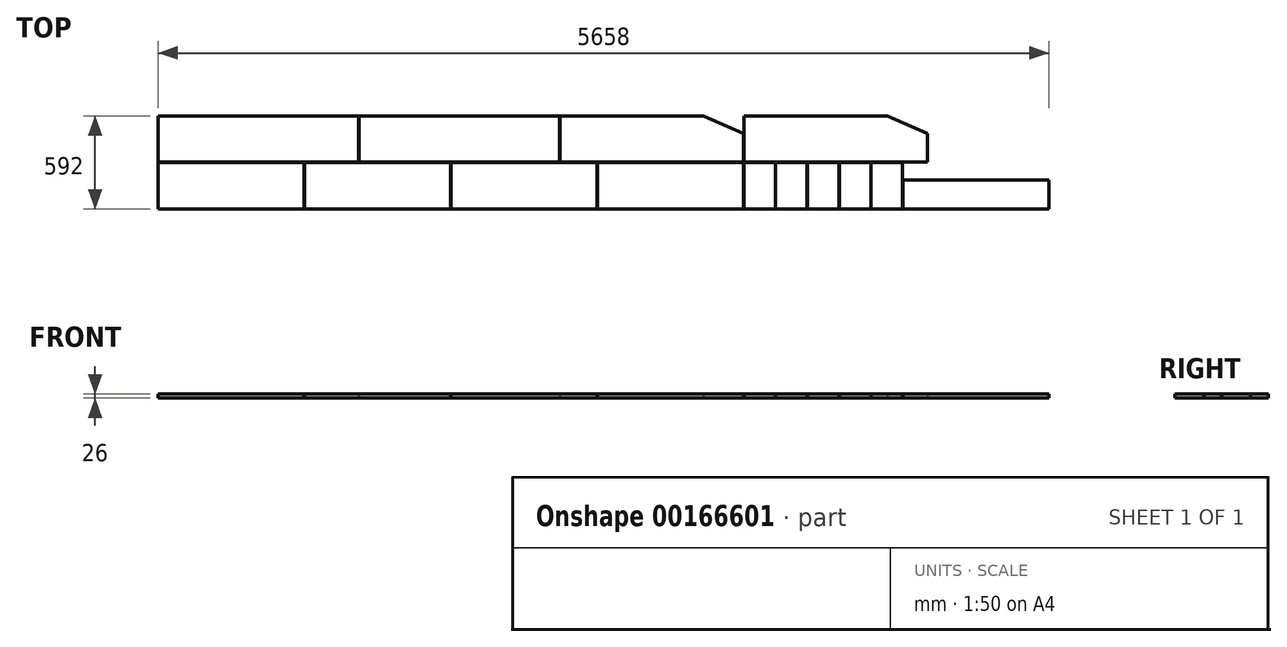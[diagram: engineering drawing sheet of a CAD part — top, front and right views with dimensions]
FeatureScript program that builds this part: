
annotation { "Feature Type Name" : "Feature", "Feature Type Description" : "" }
export const myFeature = defineFeature(function(context is Context, id is Id, definition is map)
    precondition{}
    {
        {
            var Q0;
            Q0=qCreatedBy(makeId("Top.planeOp"),FACE);
            var sketch = newSketch(context, id + "F0", { "sketchPlane" : qUnion([Q0])});
            skLineSegment(sketch, "E0.bottom", {"start": v(0, 0) * mm, "end": v(928, 0) * mm});
            skLineSegment(sketch, "E0.top", {"start": v(0, 295) * mm, "end": v(928, 295) * mm});
            skLineSegment(sketch, "E0.left", {"start": v(0, 0) * mm, "end": v(0, 295) * mm});
            skLineSegment(sketch, "E0.right", {"start": v(928, 0) * mm, "end": v(928, 295) * mm});
            skLineSegment(sketch, "E1.1.0.0", {"start": v(930, 295) * mm, "end": v(1858, 295) * mm});
            skLineSegment(sketch, "E1.1.0.1", {"start": v(930, 0) * mm, "end": v(930, 295) * mm});
            skLineSegment(sketch, "E1.1.0.2", {"start": v(1858, 0) * mm, "end": v(1858, 295) * mm});
            skLineSegment(sketch, "E1.1.0.3", {"start": v(930, 0) * mm, "end": v(1858, 0) * mm});
            skLineSegment(sketch, "E1.2.0.0", {"start": v(1860, 295) * mm, "end": v(2788, 295) * mm});
            skLineSegment(sketch, "E1.2.0.1", {"start": v(1860, 0) * mm, "end": v(1860, 295) * mm});
            skLineSegment(sketch, "E1.2.0.2", {"start": v(2788, 0) * mm, "end": v(2788, 295) * mm});
            skLineSegment(sketch, "E1.2.0.3", {"start": v(1860, 0) * mm, "end": v(2788, 0) * mm});
            skLineSegment(sketch, "E1.3.0.0", {"start": v(2790, 295) * mm, "end": v(3718, 295) * mm});
            skLineSegment(sketch, "E1.3.0.1", {"start": v(2790, 0) * mm, "end": v(2790, 295) * mm});
            skLineSegment(sketch, "E1.3.0.2", {"start": v(3718, 0) * mm, "end": v(3718, 295) * mm});
            skLineSegment(sketch, "E1.3.0.3", {"start": v(2790, 0) * mm, "end": v(3718, 0) * mm});
            skLineSegment(sketch, "E1.direction1", {"start": v(0, 0) * mm, "end": v(930, 0) * mm, "construction": true});
            skLineSegment(sketch, "E2.bottom", {"start": v(0, 297) * mm, "end": v(1274, 297) * mm});
            skLineSegment(sketch, "E2.top", {"start": v(0, 592) * mm, "end": v(1274, 592) * mm});
            skLineSegment(sketch, "E2.left", {"start": v(0, 297) * mm, "end": v(0, 592) * mm});
            skLineSegment(sketch, "E2.right", {"start": v(1274, 297) * mm, "end": v(1274, 592) * mm});
            skLineSegment(sketch, "E3.1.0.0", {"start": v(1276, 297) * mm, "end": v(2550, 297) * mm});
            skLineSegment(sketch, "E3.1.0.1", {"start": v(1276, 297) * mm, "end": v(1276, 592) * mm});
            skLineSegment(sketch, "E3.1.0.2", {"start": v(2550, 297) * mm, "end": v(2550, 592) * mm});
            skLineSegment(sketch, "E3.1.0.3", {"start": v(1276, 592) * mm, "end": v(2550, 592) * mm});
            skLineSegment(sketch, "E3.direction1", {"start": v(0, 297) * mm, "end": v(1276, 297) * mm, "construction": true});
            skLineSegment(sketch, "E4.bottom", {"start": v(2552, 297) * mm, "end": v(3718, 297) * mm});
            skLineSegment(sketch, "E4.top", {"start": v(2552, 592) * mm, "end": v(3464, 592) * mm});
            skLineSegment(sketch, "E4.left", {"start": v(2552, 297) * mm, "end": v(2552, 592) * mm});
            skLineSegment(sketch, "E4.right", {"start": v(3718, 297) * mm, "end": v(3718, 480) * mm});
            skLineSegment(sketch, "E5.bottom", {"start": v(3720, 0) * mm, "end": v(3920, 0) * mm});
            skLineSegment(sketch, "E5.top", {"start": v(3720, 295) * mm, "end": v(3920, 295) * mm});
            skLineSegment(sketch, "E5.left", {"start": v(3720, 0) * mm, "end": v(3720, 295) * mm});
            skLineSegment(sketch, "E5.right", {"start": v(3920, 0) * mm, "end": v(3920, 295) * mm});
            skLineSegment(sketch, "E6.1.0.0", {"start": v(4122, 0) * mm, "end": v(4122, 295) * mm});
            skLineSegment(sketch, "E6.1.0.1", {"start": v(3922, 295) * mm, "end": v(4122, 295) * mm});
            skLineSegment(sketch, "E6.1.0.2", {"start": v(3922, 0) * mm, "end": v(3922, 295) * mm});
            skLineSegment(sketch, "E6.1.0.3", {"start": v(3922, 0) * mm, "end": v(4122, 0) * mm});
            skLineSegment(sketch, "E6.2.0.0", {"start": v(4324, 0) * mm, "end": v(4324, 295) * mm});
            skLineSegment(sketch, "E6.2.0.1", {"start": v(4124, 295) * mm, "end": v(4324, 295) * mm});
            skLineSegment(sketch, "E6.2.0.2", {"start": v(4124, 0) * mm, "end": v(4124, 295) * mm});
            skLineSegment(sketch, "E6.2.0.3", {"start": v(4124, 0) * mm, "end": v(4324, 0) * mm});
            skLineSegment(sketch, "E6.3.0.0", {"start": v(4526, 0) * mm, "end": v(4526, 295) * mm});
            skLineSegment(sketch, "E6.3.0.1", {"start": v(4326, 295) * mm, "end": v(4526, 295) * mm});
            skLineSegment(sketch, "E6.3.0.2", {"start": v(4326, 0) * mm, "end": v(4326, 295) * mm});
            skLineSegment(sketch, "E6.3.0.3", {"start": v(4326, 0) * mm, "end": v(4526, 0) * mm});
            skLineSegment(sketch, "E6.4.0.0", {"start": v(4728, 0) * mm, "end": v(4728, 295) * mm});
            skLineSegment(sketch, "E6.4.0.1", {"start": v(4528, 295) * mm, "end": v(4728, 295) * mm});
            skLineSegment(sketch, "E6.4.0.2", {"start": v(4528, 0) * mm, "end": v(4528, 295) * mm});
            skLineSegment(sketch, "E6.4.0.3", {"start": v(4528, 0) * mm, "end": v(4728, 0) * mm});
            skLineSegment(sketch, "E6.direction1", {"start": v(3720, 0) * mm, "end": v(3922, 0) * mm, "construction": true});
            skLineSegment(sketch, "E7.bottom", {"start": v(4730, 0) * mm, "end": v(5658, 0) * mm});
            skLineSegment(sketch, "E7.top", {"start": v(4730, 183) * mm, "end": v(5658, 183) * mm});
            skLineSegment(sketch, "E7.left", {"start": v(4730, 0) * mm, "end": v(4730, 183) * mm});
            skLineSegment(sketch, "E7.right", {"start": v(5658, 0) * mm, "end": v(5658, 183) * mm});
            skLineSegment(sketch, "E8", {"start": v(3718, 480) * mm, "end": v(3464, 592) * mm});
            skLineSegment(sketch, "E9.1.0.0", {"start": v(4886, 480) * mm, "end": v(4632, 592) * mm});
            skLineSegment(sketch, "E9.1.0.1", {"start": v(3720, 592) * mm, "end": v(4632, 592) * mm});
            skLineSegment(sketch, "E9.1.0.2", {"start": v(4886, 297) * mm, "end": v(4886, 480) * mm});
            skLineSegment(sketch, "E9.1.0.3", {"start": v(3720, 297) * mm, "end": v(4886, 297) * mm});
            skLineSegment(sketch, "E9.1.0.4", {"start": v(3720, 297) * mm, "end": v(3720, 592) * mm});
            skLineSegment(sketch, "E9.direction1", {"start": v(2552, 297) * mm, "end": v(3720, 297) * mm, "construction": true});
            skSolve(sketch);
        }
        {
            var Q0;
            Q0 = qSketchRegion(id + "F0", true);
            extrude(context, id + "F1", {"entities" : qUnion([Q0]), "depth" : 26 * mm});
        }
    });
